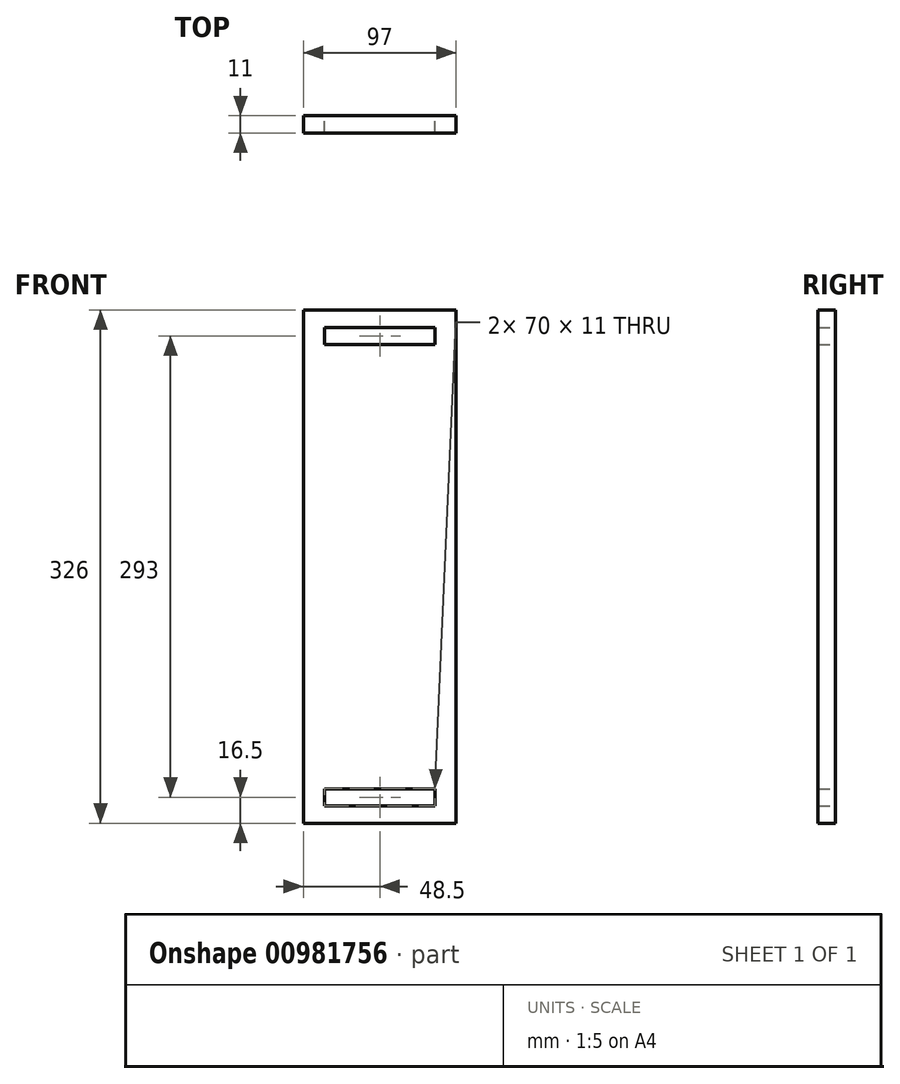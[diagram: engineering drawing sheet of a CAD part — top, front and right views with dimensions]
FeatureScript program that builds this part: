
annotation { "Feature Type Name" : "Feature", "Feature Type Description" : "" }
export const myFeature = defineFeature(function(context is Context, id is Id, definition is map)
    precondition{}
    {
        {
            var Q0;
            Q0=qCreatedBy(makeId("Front.planeOp"),FACE);
            var sketch = newSketch(context, id + "F0", { "sketchPlane" : qUnion([Q0])});
            skLineSegment(sketch, "E0", {"start": v(48.5, 163) * mm, "end": v(-48.5, 163) * mm});
            skLineSegment(sketch, "E1", {"start": v(-48.5, 163) * mm, "end": v(-48.5, -163) * mm});
            skLineSegment(sketch, "E2", {"start": v(48.5, 163) * mm, "end": v(48.5, -163) * mm});
            skLineSegment(sketch, "E3", {"start": v(48.5, -163) * mm, "end": v(-48.5, -163) * mm});
            skLineSegment(sketch, "E4", {"start": v(35, 152) * mm, "end": v(-35, 152) * mm});
            skLineSegment(sketch, "E5", {"start": v(35, 141) * mm, "end": v(-35, 141) * mm});
            skLineSegment(sketch, "E6", {"start": v(35, -141) * mm, "end": v(-35, -141) * mm});
            skLineSegment(sketch, "E7", {"start": v(35, -152) * mm, "end": v(-35, -152) * mm});
            skLineSegment(sketch, "E8", {"start": v(35, -152) * mm, "end": v(35, -141) * mm});
            skLineSegment(sketch, "E9", {"start": v(35, 141) * mm, "end": v(35, 152) * mm});
            skLineSegment(sketch, "E10", {"start": v(-35, -152) * mm, "end": v(-35, -141) * mm});
            skLineSegment(sketch, "E11", {"start": v(-35, 141) * mm, "end": v(-35, 152) * mm});
            skSolve(sketch);
        }
        {
            var Q0;
            Q0=makeQuery(id+"F0.imprint","IMPRINT",FACE,{"disambiguationData":[TD([[makeQuery(id+"F0.imprint","IMPRINT",EDGE,{"derivedFrom":sQuery(id+"F0.wireOp",EDGE,"E0")}),1.0]])]});
            extrude(context, id + "F1", {"entities" : qUnion([Q0]), "depth" : 11 * mm, "offsetDistance" : 25 * mm});
        }
    });
